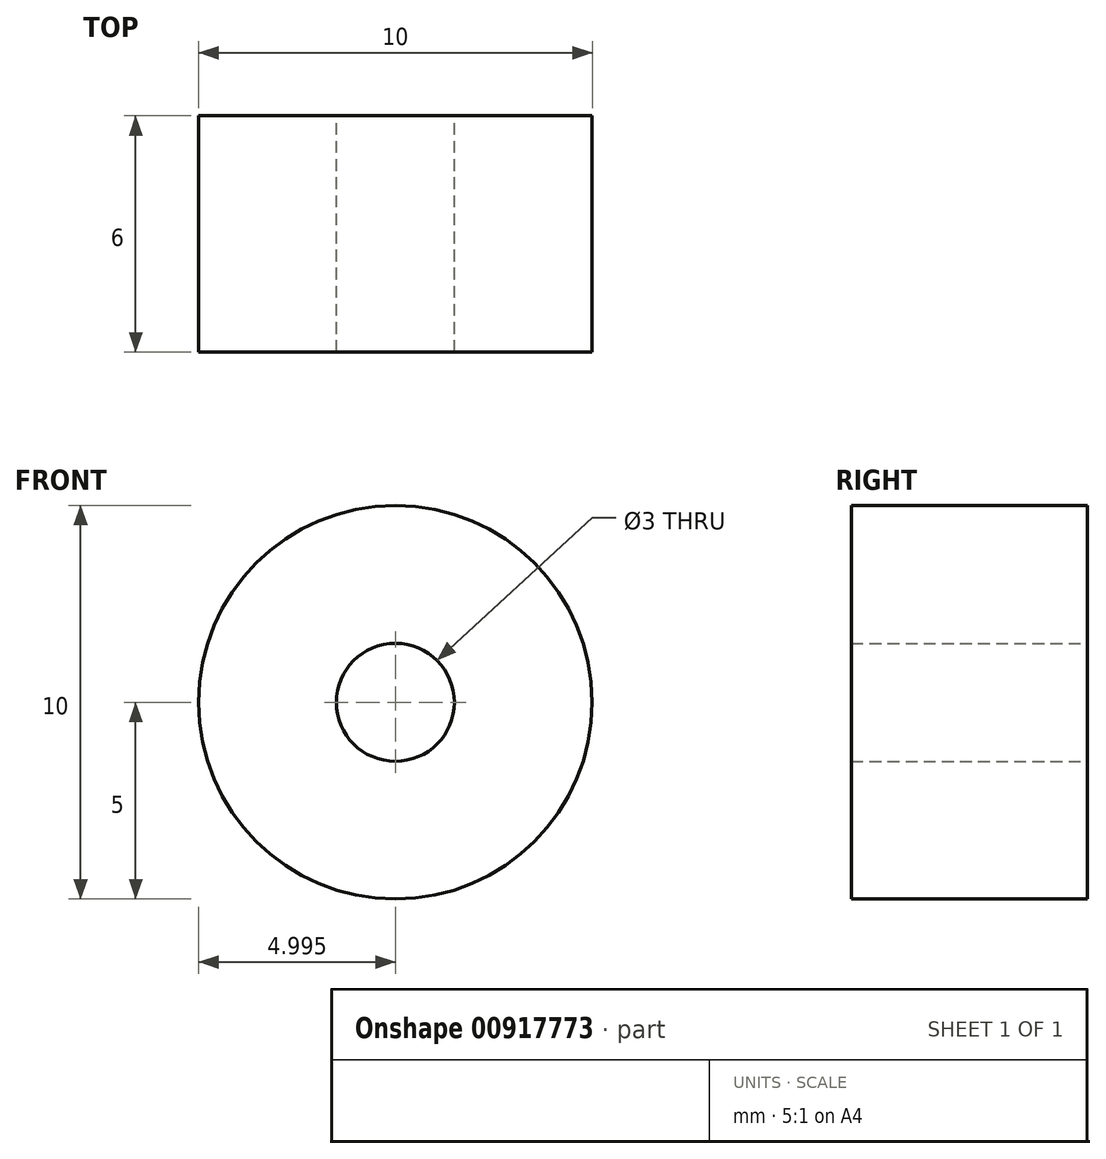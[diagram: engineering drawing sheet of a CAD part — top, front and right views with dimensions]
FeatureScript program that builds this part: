
annotation { "Feature Type Name" : "Feature", "Feature Type Description" : "" }
export const myFeature = defineFeature(function(context is Context, id is Id, definition is map)
    precondition{}
    {
        {
            var Q0;
            Q0=qCreatedBy(makeId("Front.planeOp"),FACE);
            var sketch = newSketch(context, id + "F0", { "sketchPlane" : qUnion([Q0])});
            skCircle(sketch, "E0", {"center": v(0.96, 0) * mm, "radius": 5 * mm});
            skCircle(sketch, "E1", {"center": v(0.96, 0) * mm, "radius": 1.5 * mm});
            skSolve(sketch);
        }
        {
            var Q0;
            Q0=makeQuery(id+"F0.imprint","IMPRINT",FACE,{"disambiguationData":[TD([[makeQuery(id+"F0.imprint","IMPRINT",EDGE,{"derivedFrom":sQuery(id+"F0.wireOp",EDGE,"E0")}),1.0]])]});
            extrude(context, id + "F1", {"entities" : qUnion([Q0]), "depth" : 6 * mm, "offsetDistance" : 25 * mm});
        }
    });
